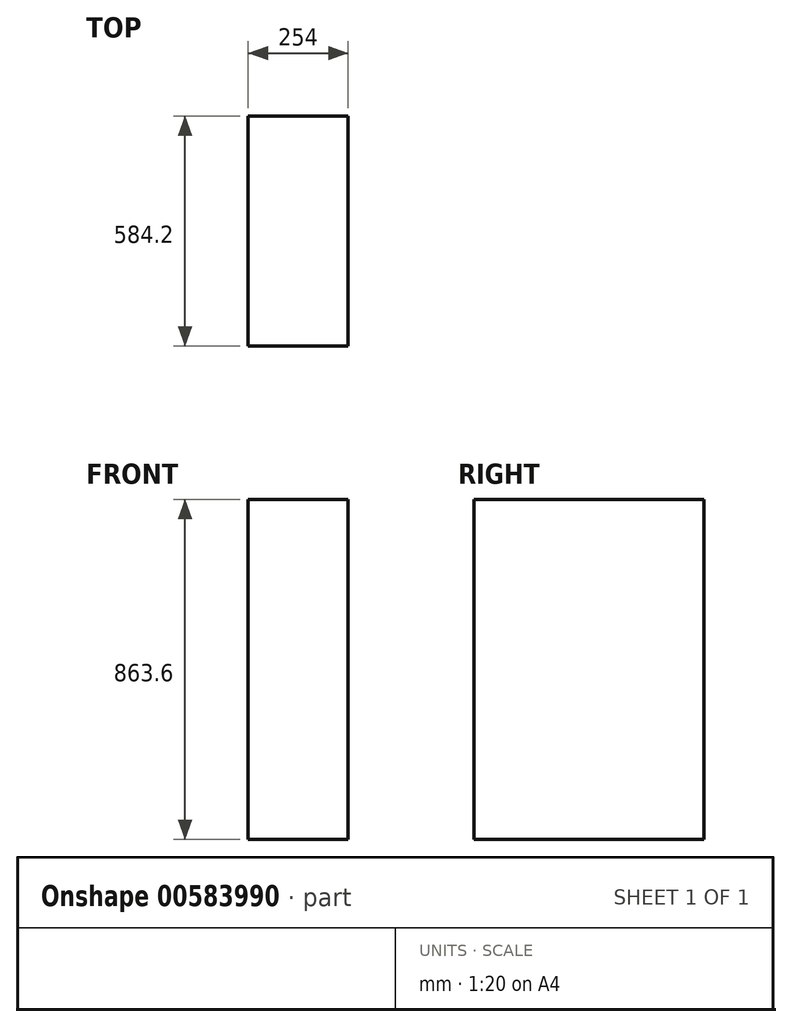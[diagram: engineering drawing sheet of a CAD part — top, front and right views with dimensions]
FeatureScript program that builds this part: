
annotation { "Feature Type Name" : "Feature", "Feature Type Description" : "" }
export const myFeature = defineFeature(function(context is Context, id is Id, definition is map)
    precondition{}
    {
        {
            var Q0;
            Q0=qCreatedBy(makeId("Top.planeOp"),FACE);
            var sketch = newSketch(context, id + "F0", { "sketchPlane" : qUnion([Q0])});
            skLineSegment(sketch, "E0.bottom", {"start": v(-128.05, 482.35) * mm, "end": v(125.95, 482.35) * mm});
            skLineSegment(sketch, "E0.top", {"start": v(-128.05, -101.85) * mm, "end": v(125.95, -101.85) * mm});
            skLineSegment(sketch, "E0.left", {"start": v(-128.05, 482.35) * mm, "end": v(-128.05, -101.85) * mm});
            skLineSegment(sketch, "E0.right", {"start": v(125.95, 482.35) * mm, "end": v(125.95, -101.85) * mm});
            skSolve(sketch);
        }
        {
            var Q0;
            Q0=makeQuery(id+"F0.imprint","IMPRINT",FACE,{"disambiguationData":[TD([[makeQuery(id+"F0.imprint","IMPRINT",EDGE,{"derivedFrom":sQuery(id+"F0.wireOp",EDGE,"E0.bottom")}),-1.0]])]});
            extrude(context, id + "F1", {"entities" : qUnion([Q0]), "depth" : 863.6 * mm, "offsetDistance" : 25.4 * mm});
        }
    });
